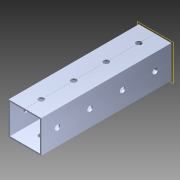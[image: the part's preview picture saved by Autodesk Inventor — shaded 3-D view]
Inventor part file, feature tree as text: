
AUTODESK INVENTOR PART (.ipt)
format: ipt  version: 2014 SP1 (Build 180222100, 222)  size: 1,132,544 bytes
history: native  units: in
note: dims shown in document units (in); Inventor stores cm internally (conversion verified against a paired STEP export)
features: pattern_circular x1, other x1, plane x1, extrude x1, imported_body x1, sketch x1
ambient origin geometry x8: Origin, YZ Plane, XZ Plane, XY Plane, X Axis, Y Axis, Z Axis, Center Point
bodies: Body1 (feature_tree)
feature tree (6):
  pattern_circular  "CirPattern2"
  other  "217-3426-STEP1"
  plane  "Work Plane1"
  extrude  "Extrusion1"  Depth=3937.0079in TaperAngle=0.0deg
  imported_body  "Base1"
  sketch  "Sketch1"  dims[d0=-4.0in d1=3937.0079in d2=0.0in]
